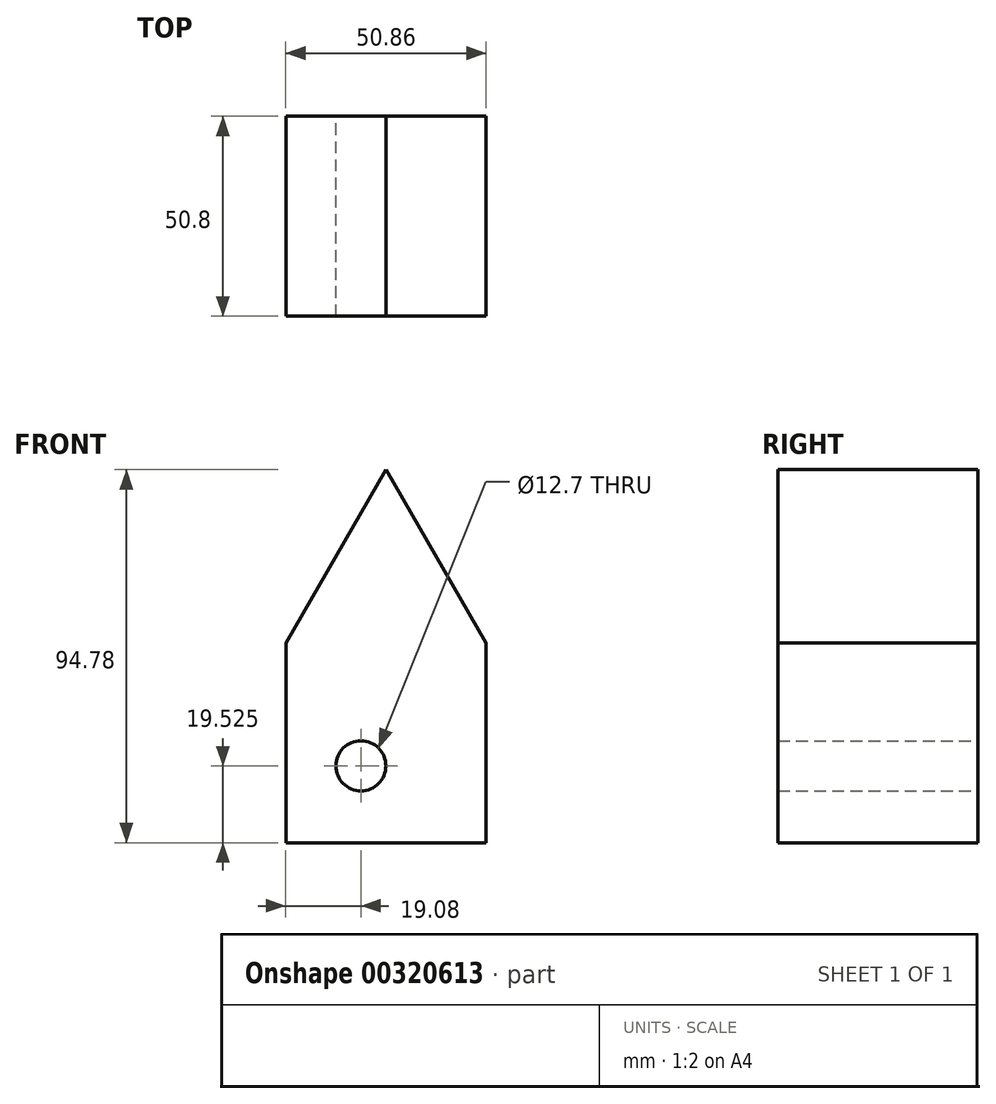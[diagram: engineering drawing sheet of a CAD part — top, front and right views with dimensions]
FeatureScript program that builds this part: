
annotation { "Feature Type Name" : "Feature", "Feature Type Description" : "" }
export const myFeature = defineFeature(function(context is Context, id is Id, definition is map)
    precondition{}
    {
        {
            var Q0;
            Q0=qCreatedBy(makeId("Front.planeOp"),FACE);
            var sketch = newSketch(context, id + "F0", { "sketchPlane" : qUnion([Q0])});
            skLineSegment(sketch, "E0.right", {"start": v(-25.43, -25.4) * mm, "end": v(-25.4, 25.38) * mm});
            skPoint(sketch, "E0.middle", {"position": v(0, 0) * mm});
            skLineSegment(sketch, "E1.left", {"start": v(-25.43, -25.4) * mm, "end": v(-25.4, -5.87) * mm});
            skLineSegment(sketch, "E2", {"start": v(0, 69.38) * mm, "end": v(25.43, 25.4) * mm});
            skCircle(sketch, "E3", {"center": v(-6.35, -5.87) * mm, "radius": 6.35 * mm});
            skLineSegment(sketch, "E4", {"start": v(-25.4, 25.38) * mm, "end": v(0, 69.38) * mm});
            skLineSegment(sketch, "E5", {"start": v(-25.43, -25.4) * mm, "end": v(25.37, -25.4) * mm});
            skLineSegment(sketch, "E6", {"start": v(25.37, -25.4) * mm, "end": v(25.43, 25.4) * mm});
            skSolve(sketch);
        }
        {
            var Q0;
            Q0 = qSketchRegion(id + "F0", true);
            extrude(context, id + "F1", {"entities" : qUnion([Q0]), "depth" : 50.8 * mm});
        }
    });
